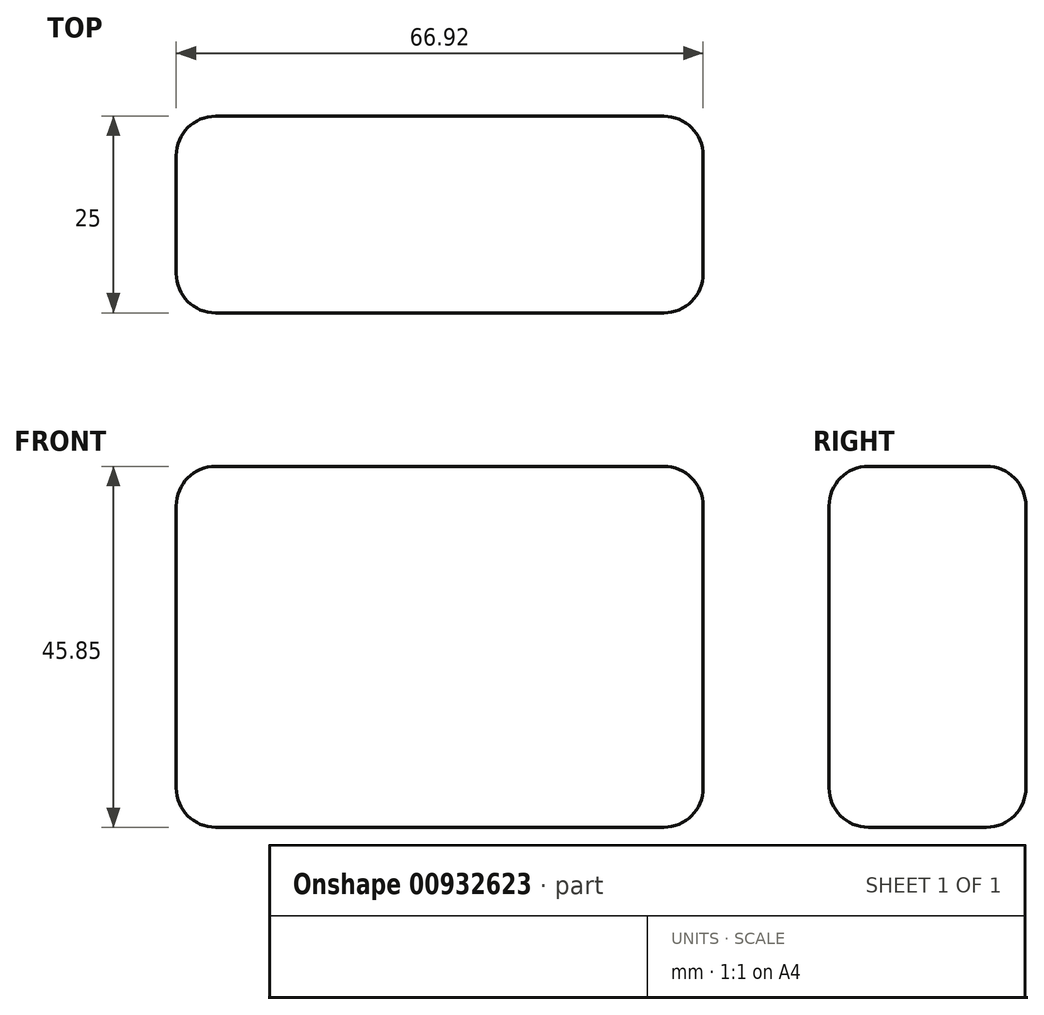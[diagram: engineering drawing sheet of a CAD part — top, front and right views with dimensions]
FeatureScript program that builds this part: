
annotation { "Feature Type Name" : "Feature", "Feature Type Description" : "" }
export const myFeature = defineFeature(function(context is Context, id is Id, definition is map)
    precondition{}
    {
        {
            var Q0;
            Q0=qCreatedBy(makeId("Front.planeOp"),FACE);
            var sketch = newSketch(context, id + "F0", { "sketchPlane" : qUnion([Q0])});
            skLineSegment(sketch, "E0.bottom", {"start": v(-114.26, 53.66) * mm, "end": v(-47.34, 53.66) * mm});
            skLineSegment(sketch, "E0.top", {"start": v(-114.26, 7.81) * mm, "end": v(-47.34, 7.81) * mm});
            skLineSegment(sketch, "E0.left", {"start": v(-114.26, 53.66) * mm, "end": v(-114.26, 7.81) * mm});
            skLineSegment(sketch, "E0.right", {"start": v(-47.34, 53.66) * mm, "end": v(-47.34, 7.81) * mm});
            skSolve(sketch);
        }
        {
            var Q0;
            Q0 = qSketchRegion(id + "F0", true);
            extrude(context, id + "F1", {"entities" : qUnion([Q0]), "depth" : 25 * mm, "offsetDistance" : 25 * mm});
        }
        {
            var Q0;
            Q0=makeQuery(id+"F1.opExtrude","SWEPT_EDGE",EDGE,{"disambiguationData":[OSD([sQuery(id+"F0.wireOp",EDGE,"E0.bottom"),sQuery(id+"F0.wireOp",EDGE,"E0.left")])]});
            var Q1;
            Q1=makeQuery(id+"F1.opExtrude","SWEPT_EDGE",EDGE,{"disambiguationData":[OSD([sQuery(id+"F0.wireOp",EDGE,"E0.bottom"),sQuery(id+"F0.wireOp",EDGE,"E0.right")])]});
            var Q2;
            Q2=makeQuery(id+"F1.opExtrude","SWEPT_EDGE",EDGE,{"disambiguationData":[OSD([sQuery(id+"F0.wireOp",EDGE,"E0.top"),sQuery(id+"F0.wireOp",EDGE,"E0.right")])]});
            var Q3;
            Q3=makeQuery(id+"F1.opExtrude","CAP_EDGE",EDGE,{"disambiguationData":[OSD([sQuery(id+"F0.wireOp",EDGE,"E0.bottom")])],"isStart":false});
            var Q4;
            Q4=makeQuery(id+"F1.opExtrude","CAP_EDGE",EDGE,{"disambiguationData":[OSD([sQuery(id+"F0.wireOp",EDGE,"E0.top")])],"isStart":false});
            var Q5;
            Q5=makeQuery(id+"F1.opExtrude","SWEPT_EDGE",EDGE,{"disambiguationData":[OSD([sQuery(id+"F0.wireOp",EDGE,"E0.top"),sQuery(id+"F0.wireOp",EDGE,"E0.left")])]});
            var Q6;
            Q6=makeQuery(id+"F1.opExtrude","CAP_EDGE",EDGE,{"disambiguationData":[OSD([sQuery(id+"F0.wireOp",EDGE,"E0.bottom")])],"isStart":true});
            var Q7;
            Q7=makeQuery(id+"F1.opExtrude","CAP_EDGE",EDGE,{"disambiguationData":[OSD([sQuery(id+"F0.wireOp",EDGE,"E0.top")])],"isStart":true});
            var Q8;
            Q8=makeQuery(id+"F1.opExtrude","CAP_EDGE",EDGE,{"disambiguationData":[OSD([sQuery(id+"F0.wireOp",EDGE,"E0.right")])],"isStart":true});
            var Q9;
            Q9=makeQuery(id+"F1.opExtrude","CAP_EDGE",EDGE,{"disambiguationData":[OSD([sQuery(id+"F0.wireOp",EDGE,"E0.right")])],"isStart":false});
            var Q10;
            Q10=makeQuery(id+"F1.opExtrude","CAP_EDGE",EDGE,{"disambiguationData":[OSD([sQuery(id+"F0.wireOp",EDGE,"E0.left")])],"isStart":true});
            var Q11;
            Q11=makeQuery(id+"F1.opExtrude","CAP_EDGE",EDGE,{"disambiguationData":[OSD([sQuery(id+"F0.wireOp",EDGE,"E0.left")])],"isStart":false});
            fillet(context, id + "F2", {"entities" : qUnion([Q0, Q1, Q2, Q3, Q4, Q5, Q6, Q7, Q8, Q9, Q10, Q11]), "radius" : 5 * mm, "tangentPropagation" : true, "allowEdgeOverflow" : false});
        }
    });
